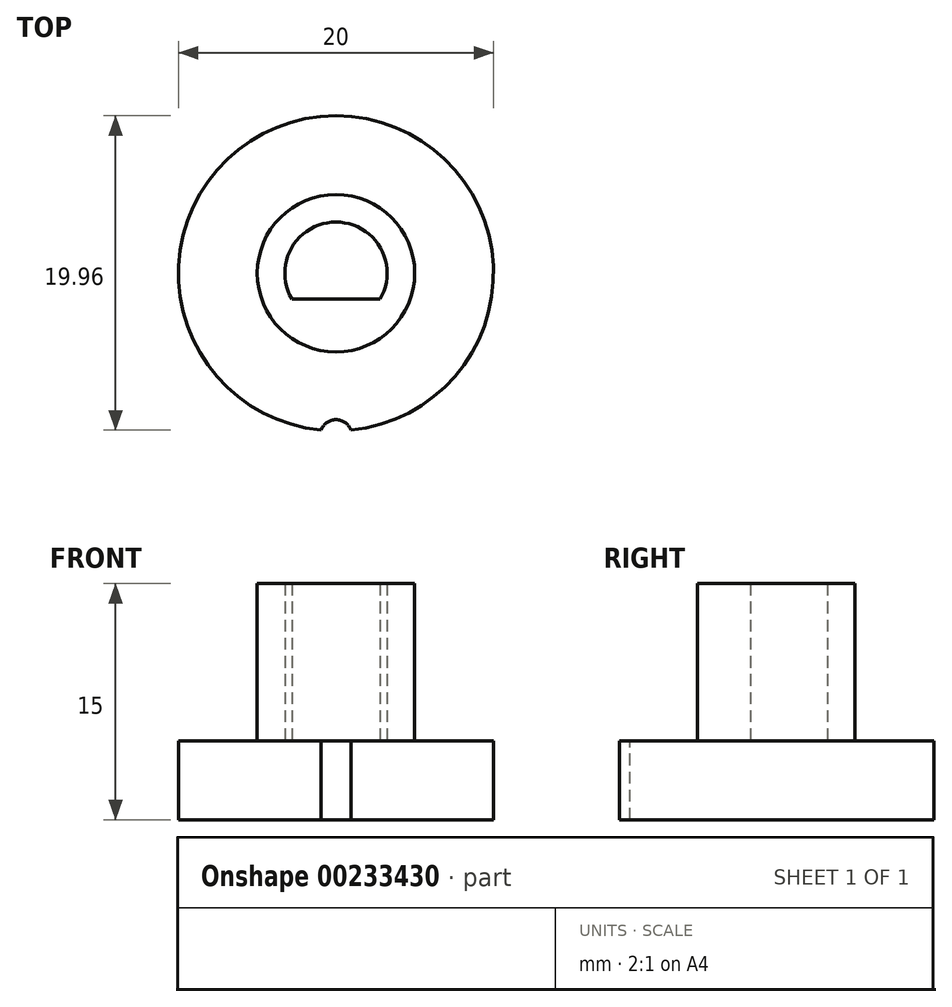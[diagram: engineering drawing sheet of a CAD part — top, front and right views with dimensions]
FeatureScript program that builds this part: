
annotation { "Feature Type Name" : "Feature", "Feature Type Description" : "" }
export const myFeature = defineFeature(function(context is Context, id is Id, definition is map)
    precondition{}
    {
        {
            var Q0;
            Q0=qCreatedBy(makeId("Top.planeOp"),FACE);
            var sketch = newSketch(context, id + "F0", { "sketchPlane" : qUnion([Q0])});
            skCircle(sketch, "E0", {"center": v(0, 0) * mm, "radius": 10 * mm});
            skSolve(sketch);
        }
        {
            var Q0;
            Q0=makeQuery(id+"F0.imprint","IMPRINT",FACE,{"disambiguationData":[TD([[makeQuery(id+"F0.imprint","IMPRINT",EDGE,{"derivedFrom":sQuery(id+"F0.wireOp",EDGE,"E0")}),1.0]])]});
            var Q1;
            Q1=sQuery(id+"F0.wireOp",EDGE,"E0");
            extrude(context, id + "F1", {"entities" : qUnion([Q0]), "surfaceEntities" : qUnion([Q1]), "depth" : 5 * mm});
        }
        {
            var Q0;
            Q0=makeQuery(id+"F1.opExtrude","CAP_FACE",FACE,{"disambiguationData":[OSD([sQuery(id+"F0.wireOp",EDGE,"E0")])],"isStart":false});
            var sketch = newSketch(context, id + "F2", { "sketchPlane" : qUnion([Q0])});
            skCircle(sketch, "E1", {"center": v(0, -10.3) * mm, "radius": 1 * mm});
            skSolve(sketch);
        }
        {
            var Q0;
            {var subQ0=sQuery(id+"F2.wireOp",EDGE,"E1");var subQ1=makeQuery(id+"F1.opExtrude","CAP_EDGE",EDGE,{"disambiguationData":[OSD([sQuery(id+"F0.wireOp",EDGE,"E0")])],"isStart":false});var subQ2=makeQuery(id+"F2.imprint","INTERSECT",VERTEX,{"disambiguationData":[OD(0.0)],"derivedFrom":[subQ1,subQ0]});Q0=makeQuery(id+"F2.imprint","IMPRINT",FACE,{"disambiguationData":[TD([[makeQuery(id+"F2.imprint","IMPRINT",EDGE,{"disambiguationData":[TD([[subQ2,1.0]])],"derivedFrom":subQ0}),1.0]])]});}
            extrude(context, id + "F3", {"entities" : qUnion([Q0]), "operationType" : NewBodyOperationType.REMOVE, "oppositeDirection" : true, "depth" : 25 * mm});
        }
        {
            var Q0;
            Q0=qCreatedBy(makeId("Front.planeOp"),FACE);
            var sketch = newSketch(context, id + "F4", { "sketchPlane" : qUnion([Q0])});
            skLineSegment(sketch, "E2", {"start": v(0, 38.5) * mm, "end": v(0, -17.37) * mm, "construction": true});
            skSolve(sketch);
        }
        {
            var Q0;
            Q0=makeQuery(id+"F1.opExtrude","CAP_FACE",FACE,{"disambiguationData":[OSD([sQuery(id+"F0.wireOp",EDGE,"E0")])],"isStart":false});
            var sketch = newSketch(context, id + "F5", { "sketchPlane" : qUnion([Q0])});
            skCircle(sketch, "E3", {"center": v(0, 0) * mm, "radius": 5 * mm});
            skArc(sketch, "E4", {"start": v(2.8, -1.65) * mm, "mid": v(0, 3.25) * mm, "end": v(-2.8, -1.65) * mm});
            skLineSegment(sketch, "E5", {"start": v(-2.8, -1.65) * mm, "end": v(2.8, -1.65) * mm});
            skSolve(sketch);
        }
        {
            var Q0;
            Q0=makeQuery(id+"F5.imprint","IMPRINT",FACE,{"disambiguationData":[TD([[makeQuery(id+"F5.imprint","IMPRINT",EDGE,{"derivedFrom":sQuery(id+"F5.wireOp",EDGE,"E3")}),1.0]])]});
            extrude(context, id + "F6", {"entities" : qUnion([Q0]), "operationType" : NewBodyOperationType.ADD, "depth" : 10 * mm});
        }
    });
